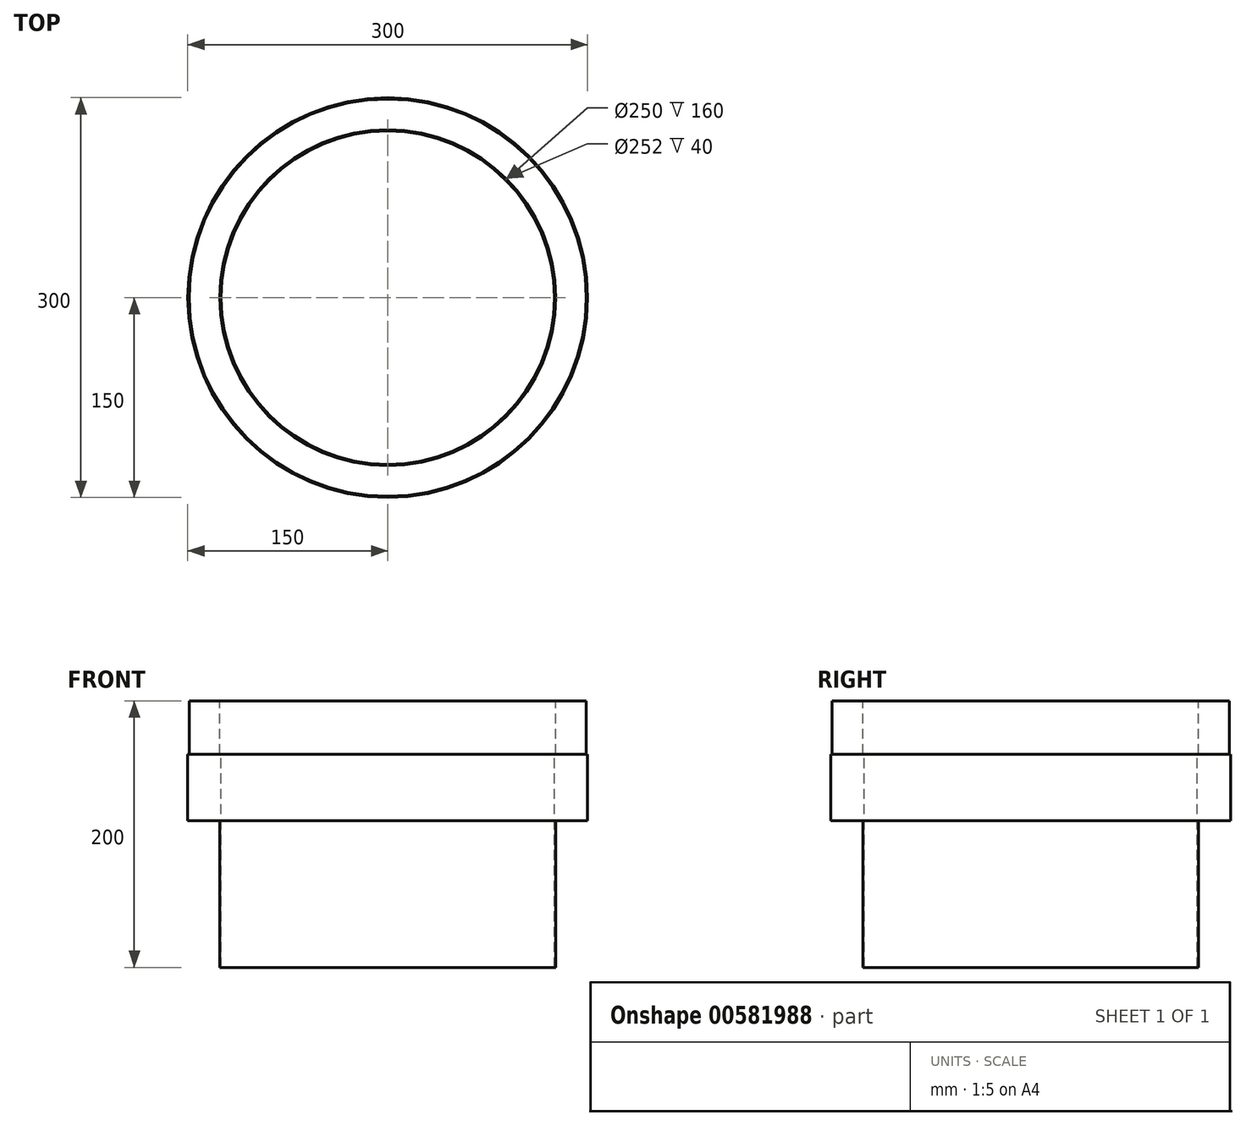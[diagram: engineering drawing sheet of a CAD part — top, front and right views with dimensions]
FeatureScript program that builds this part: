
annotation { "Feature Type Name" : "Feature", "Feature Type Description" : "" }
export const myFeature = defineFeature(function(context is Context, id is Id, definition is map)
    precondition{}
    {
        {
            var Q0;
            Q0=qCreatedBy(makeId("Front.planeOp"),FACE);
            var sketch = newSketch(context, id + "F0", { "sketchPlane" : qUnion([Q0])});
            skLineSegment(sketch, "E0", {"start": v(0, 710.75) * mm, "end": v(0, -704.58) * mm, "construction": true});
            skLineSegment(sketch, "E1", {"start": v(-125, 295.65) * mm, "end": v(-125, 410.65) * mm});
            skLineSegment(sketch, "E2", {"start": v(-125, 410.65) * mm, "end": v(-126, 410.65) * mm});
            skLineSegment(sketch, "E3", {"start": v(-149, 410.65) * mm, "end": v(-150, 410.65) * mm});
            skLineSegment(sketch, "E4", {"start": v(-150, 410.65) * mm, "end": v(-150, 360.65) * mm});
            skLineSegment(sketch, "E5", {"start": v(-150, 360.65) * mm, "end": v(-126, 360.65) * mm});
            skLineSegment(sketch, "E6", {"start": v(-126, 360.65) * mm, "end": v(-126, 295.65) * mm});
            skLineSegment(sketch, "E7", {"start": v(-149, 450.65) * mm, "end": v(-149, 410.65) * mm});
            skLineSegment(sketch, "E8", {"start": v(-149, 450.65) * mm, "end": v(-126, 450.65) * mm});
            skLineSegment(sketch, "E9", {"start": v(-126, 410.65) * mm, "end": v(-126, 450.65) * mm});
            skLineSegment(sketch, "E10", {"start": v(-125, 295.65) * mm, "end": v(-125, 250.65) * mm});
            skLineSegment(sketch, "E11", {"start": v(-126, 295.65) * mm, "end": v(-126, 250.65) * mm});
            skLineSegment(sketch, "E12", {"start": v(-126, 250.65) * mm, "end": v(-125, 250.65) * mm});
            skSolve(sketch);
        }
        {
            var Q0;
            Q0=qSketchRegion(id+"F0",true);
            var Q1;
            Q1=sQuery(id+"F0.wireOp",EDGE,"E0");
            revolve(context, id + "F1", {"entities" : qUnion([Q0]), "axis" : qUnion([Q1]), "revolveType" : RevolveType.FULL});
        }
    });
